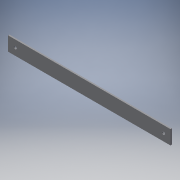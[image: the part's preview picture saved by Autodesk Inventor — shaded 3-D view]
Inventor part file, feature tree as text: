
AUTODESK INVENTOR PART (.ipt)
format: ipt  version: 2018 (Build 220112000, 112)  size: 109,056 bytes
history: native  units: in
note: dims shown in document units (in); Inventor stores cm internally (conversion verified against a paired STEP export)
features: extrude x3, sketch x3
ambient origin geometry x8: Origin, YZ Plane, XZ Plane, XY Plane, X Axis, Y Axis, Z Axis, Center Point
bodies: Solid1 (feature_tree)
feature tree (6):
  extrude  "Extrusion1"  Depth=1.0in
  extrude  "Extrusion2"  Depth=0.1in
  extrude  "Extrusion3"  Depth=1.0in
  sketch  "Sketch1"  dims[d2=11.0in d3=1.0in]
  sketch  "Sketch2"  dims[d4=0.1in d5=0.0in d6=0.2031in]
  sketch  "Sketch3"  dims[d7=0.5in d8=0.5in d9=1.0in d10=0.0in d11=0.2031in d12=0.5in d13=0.5in d14=1.0in d15=0.0in]
